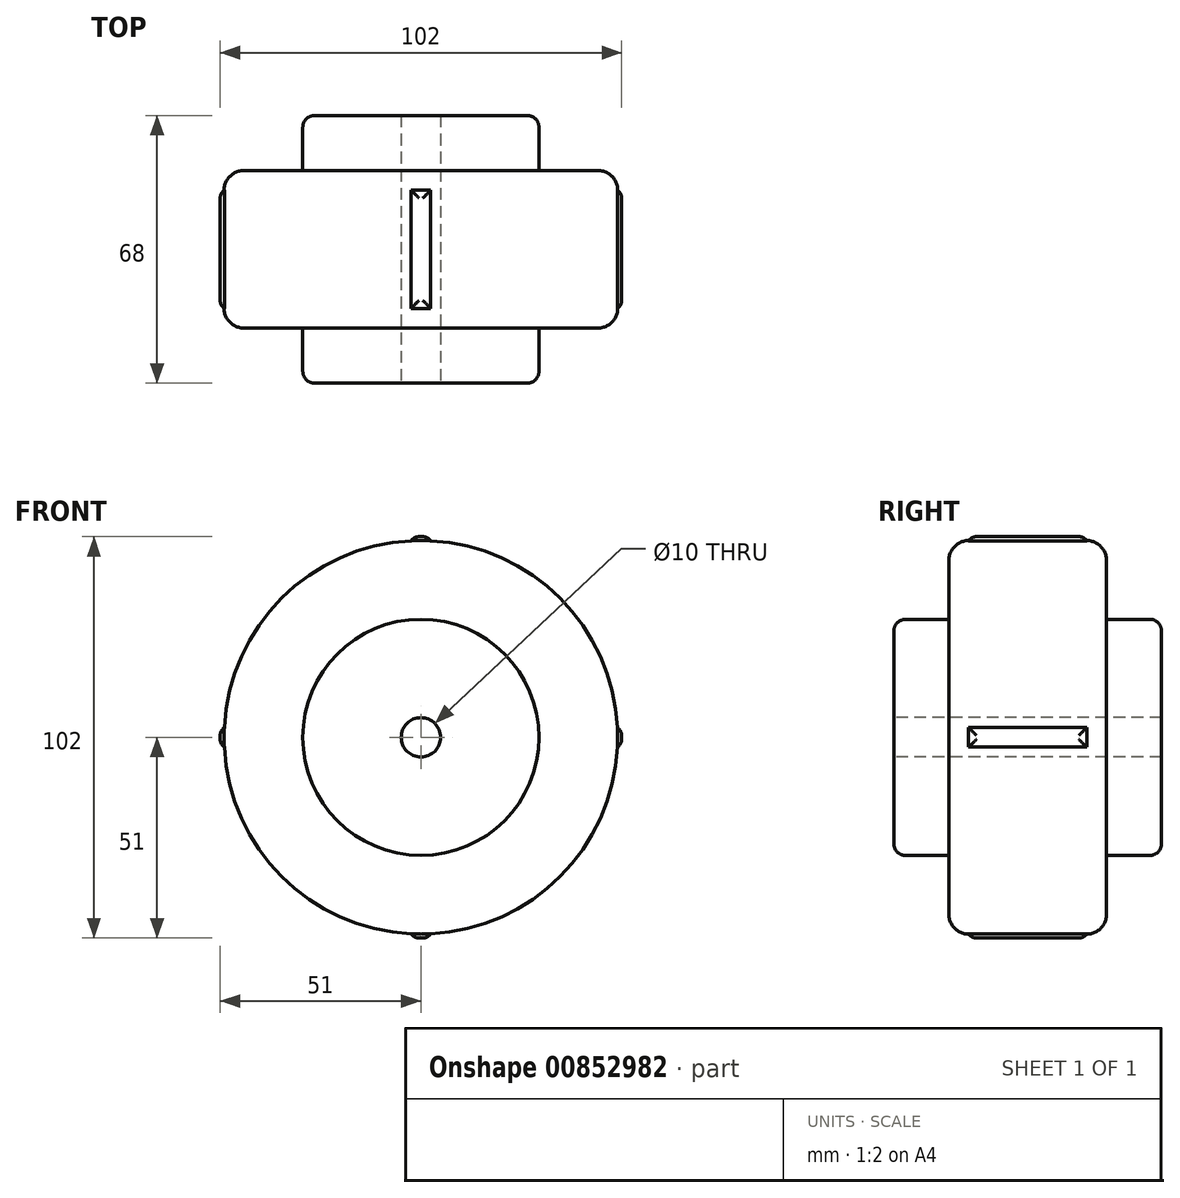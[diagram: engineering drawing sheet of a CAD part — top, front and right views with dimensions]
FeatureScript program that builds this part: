
annotation { "Feature Type Name" : "Feature", "Feature Type Description" : "" }
export const myFeature = defineFeature(function(context is Context, id is Id, definition is map)
    precondition{}
    {
        {
            var Q0;
            Q0=qCreatedBy(makeId("Front.planeOp"),FACE);
            var sketch = newSketch(context, id + "F0", { "sketchPlane" : qUnion([Q0])});
            skPoint(sketch, "E0.third.point", {"position": v(77.43, -43.66) * mm});
            skCircle(sketch, "E1", {"center": v(62.84, 12.63) * mm, "radius": 5 * mm});
            skCircle(sketch, "E2", {"center": v(62.84, 12.63) * mm, "radius": 50 * mm});
            skSolve(sketch);
        }
        {
            var Q0;
            {var subQ0=sQuery(id+"F0.wireOp",EDGE,"eTBRQ0yo-MwLn-4fZX-0Hv7-uYAHV1OEGFlB");Q0=makeQuery(id+"F0.imprint","IMPRINT",FACE,{"disambiguationData":[TD([[makeQuery(id+"F0.imprint","IMPRINT",EDGE,{"derivedFrom":subQ0}),1.0]])]});}
            var Q1;
            Q1=makeQuery(id+"F0.imprint","IMPRINT",FACE,{"disambiguationData":[TD([[makeQuery(id+"F0.imprint","IMPRINT",EDGE,{"derivedFrom":sQuery(id+"F0.wireOp",EDGE,"E1")}),-1.0]])]});
            extrude(context, id + "F1", {"entities" : qUnion([Q0, Q1]), "depth" : 40 * mm, "offsetDistance" : 25 * mm});
        }
        {
            var Q0;
            Q0=makeQuery(id+"F1.opExtrude","CAP_EDGE",EDGE,{"disambiguationData":[OSD([sQuery(id+"F0.wireOp",EDGE,"E2")])],"isStart":true});
            var Q1;
            Q1=makeQuery(id+"F1.opExtrude","CAP_EDGE",EDGE,{"disambiguationData":[OSD([sQuery(id+"F0.wireOp",EDGE,"E2")])],"isStart":false});
            fillet(context, id + "F2", {"entities" : qUnion([Q0, Q1]), "radius" : 5 * mm, "tangentPropagation" : true, "allowEdgeOverflow" : false});
        }
        {
            var Q0;
            Q0=qCreatedBy(makeId("Front.planeOp"),FACE);
            var sketch = newSketch(context, id + "F3", { "sketchPlane" : qUnion([Q0])});
            skArc(sketch, "E3", {"start": v(65.34, 62.57) * mm, "mid": v(62.84, 62.63) * mm, "end": v(60.34, 62.57) * mm});
            skArc(sketch, "E4", {"start": v(65.34, 63.57) * mm, "mid": v(62.84, 63.63) * mm, "end": v(60.34, 63.57) * mm});
            skLineSegment(sketch, "E5.top", {"start": v(62.84, 162.63) * mm, "end": v(60.34, 162.63) * mm});
            skLineSegment(sketch, "E6.top", {"start": v(12.9, 10.13) * mm, "end": v(11.9, 10.13) * mm});
            skLineSegment(sketch, "E7.trimOffspring", {"start": v(112.78, 15.13) * mm, "end": v(113.78, 15.13) * mm});
            skLineSegment(sketch, "E8.trimOffspring", {"start": v(112.78, 10.13) * mm, "end": v(113.78, 10.13) * mm});
            skArc(sketch, "E9.trimOffspring", {"start": v(113.78, 10.13) * mm, "mid": v(113.84, 12.63) * mm, "end": v(113.78, 15.13) * mm});
            skArc(sketch, "E10.trimOffspring", {"start": v(112.78, 10.13) * mm, "mid": v(112.84, 12.63) * mm, "end": v(112.78, 15.13) * mm});
            skLineSegment(sketch, "E11.trimOffspring", {"start": v(60.34, -37.3) * mm, "end": v(60.34, -38.3) * mm});
            skLineSegment(sketch, "E12.trimOffspring", {"start": v(65.34, -37.3) * mm, "end": v(65.34, -38.3) * mm});
            skPoint(sketch, "E13.trimOffspring.end.orphan", {"position": v(62.84, -132.37) * mm});
            skArc(sketch, "E14.trimOffspring", {"start": v(60.34, -38.3) * mm, "mid": v(62.84, -38.37) * mm, "end": v(65.34, -38.3) * mm});
            skArc(sketch, "E15.trimOffspring", {"start": v(60.34, -37.3) * mm, "mid": v(62.84, -37.37) * mm, "end": v(65.34, -37.3) * mm});
            skArc(sketch, "E16.trimOffspring", {"start": v(11.9, 15.13) * mm, "mid": v(11.84, 12.63) * mm, "end": v(11.9, 10.13) * mm});
            skArc(sketch, "E17.trimOffspring", {"start": v(12.9, 15.13) * mm, "mid": v(12.84, 12.63) * mm, "end": v(12.9, 10.13) * mm});
            skLineSegment(sketch, "E18.trimOffspring", {"start": v(12.9, 15.13) * mm, "end": v(11.9, 15.13) * mm});
            skLineSegment(sketch, "E19.trimOffspring", {"start": v(65.34, 62.57) * mm, "end": v(65.34, 63.57) * mm});
            skLineSegment(sketch, "E20.trimOffspring", {"start": v(60.34, 62.57) * mm, "end": v(60.34, 63.57) * mm});
            skSolve(sketch);
        }
        {
            var Q0;
            Q0=makeQuery(id+"F3.imprint","IMPRINT",FACE,{"disambiguationData":[TD([[makeQuery(id+"F3.imprint","IMPRINT",EDGE,{"derivedFrom":sQuery(id+"F3.wireOp",EDGE,"E7.trimOffspring")}),-1.0]])]});
            var Q1;
            Q1=makeQuery(id+"F3.imprint","IMPRINT",FACE,{"disambiguationData":[TD([[makeQuery(id+"F3.imprint","IMPRINT",EDGE,{"derivedFrom":sQuery(id+"F3.wireOp",EDGE,"E11.trimOffspring")}),1.0]])]});
            var Q2;
            Q2=makeQuery(id+"F3.imprint","IMPRINT",FACE,{"disambiguationData":[TD([[makeQuery(id+"F3.imprint","IMPRINT",EDGE,{"derivedFrom":sQuery(id+"F3.wireOp",EDGE,"E6.top")}),-1.0]])]});
            var Q3;
            Q3=makeQuery(id+"F3.imprint","IMPRINT",FACE,{"disambiguationData":[TD([[makeQuery(id+"F3.imprint","IMPRINT",EDGE,{"derivedFrom":sQuery(id+"F3.wireOp",EDGE,"E3")}),-1.0]])]});
            extrude(context, id + "F4", {"entities" : qUnion([Q0, Q1, Q2, Q3]), "operationType" : NewBodyOperationType.ADD, "depth" : 35 * mm, "offsetDistance" : 25 * mm, "hasSecondDirection" : true, "secondDirectionOppositeDirection" : false, "secondDirectionDepth" : 5 * mm});
        }
        {
            var Q0;
            Q0=makeQuery(id+"F4.opExtrude","SWEPT_EDGE",EDGE,{"disambiguationData":[OSD([sQuery(id+"F3.wireOp",EDGE,"E4"),sQuery(id+"F3.wireOp",EDGE,"E19.trimOffspring")])]});
            var Q1;
            Q1=makeQuery(id+"F4.opExtrude","SWEPT_EDGE",EDGE,{"disambiguationData":[OSD([sQuery(id+"F3.wireOp",EDGE,"E4"),sQuery(id+"F3.wireOp",EDGE,"E20.trimOffspring")])]});
            var Q2;
            Q2=makeQuery(id+"F4.opExtrude","SWEPT_EDGE",EDGE,{"disambiguationData":[OSD([sQuery(id+"F3.wireOp",EDGE,"E16.trimOffspring"),sQuery(id+"F3.wireOp",EDGE,"E18.trimOffspring")])]});
            var Q3;
            Q3=makeQuery(id+"F4.opExtrude","SWEPT_EDGE",EDGE,{"disambiguationData":[OSD([sQuery(id+"F3.wireOp",EDGE,"E6.top"),sQuery(id+"F3.wireOp",EDGE,"E16.trimOffspring")])]});
            var Q4;
            Q4=makeQuery(id+"F4.opExtrude","SWEPT_EDGE",EDGE,{"disambiguationData":[OSD([sQuery(id+"F3.wireOp",EDGE,"E11.trimOffspring"),sQuery(id+"F3.wireOp",EDGE,"E14.trimOffspring")])]});
            var Q5;
            Q5=makeQuery(id+"F4.opExtrude","SWEPT_EDGE",EDGE,{"disambiguationData":[OSD([sQuery(id+"F3.wireOp",EDGE,"E12.trimOffspring"),sQuery(id+"F3.wireOp",EDGE,"E14.trimOffspring")])]});
            var Q6;
            Q6=makeQuery(id+"F4.opExtrude","SWEPT_EDGE",EDGE,{"disambiguationData":[OSD([sQuery(id+"F3.wireOp",EDGE,"E8.trimOffspring"),sQuery(id+"F3.wireOp",EDGE,"E9.trimOffspring")])]});
            var Q7;
            Q7=makeQuery(id+"F4.opExtrude","SWEPT_EDGE",EDGE,{"disambiguationData":[OSD([sQuery(id+"F3.wireOp",EDGE,"E7.trimOffspring"),sQuery(id+"F3.wireOp",EDGE,"E9.trimOffspring")])]});
            fillet(context, id + "F5", {"entities" : qUnion([Q0, Q1, Q2, Q3, Q4, Q5, Q6, Q7]), "radius" : 2.5 * mm, "tangentPropagation" : true, "allowEdgeOverflow" : false});
        }
        {
            var Q0;
            Q0=makeQuery(id+"F4.opExtrude","CAP_EDGE",EDGE,{"disambiguationData":[OSD([sQuery(id+"F3.wireOp",EDGE,"E9.trimOffspring")])],"isStart":true});
            var Q1;
            Q1=makeQuery(id+"F4.opExtrude","CAP_EDGE",EDGE,{"disambiguationData":[OSD([sQuery(id+"F3.wireOp",EDGE,"E4")])],"isStart":true});
            var Q2;
            Q2=makeQuery(id+"F4.opExtrude","CAP_EDGE",EDGE,{"disambiguationData":[OSD([sQuery(id+"F3.wireOp",EDGE,"E4")])],"isStart":false});
            var Q3;
            Q3=makeQuery(id+"F4.opExtrude","CAP_EDGE",EDGE,{"disambiguationData":[OSD([sQuery(id+"F3.wireOp",EDGE,"E9.trimOffspring")])],"isStart":false});
            var Q4;
            Q4=makeQuery(id+"F4.opExtrude","CAP_EDGE",EDGE,{"disambiguationData":[OSD([sQuery(id+"F3.wireOp",EDGE,"E14.trimOffspring")])],"isStart":false});
            var Q5;
            Q5=makeQuery(id+"F4.opExtrude","CAP_EDGE",EDGE,{"disambiguationData":[OSD([sQuery(id+"F3.wireOp",EDGE,"E14.trimOffspring")])],"isStart":true});
            var Q6;
            Q6=makeQuery(id+"F4.opExtrude","CAP_EDGE",EDGE,{"disambiguationData":[OSD([sQuery(id+"F3.wireOp",EDGE,"E16.trimOffspring")])],"isStart":false});
            var Q7;
            Q7=makeQuery(id+"F4.opExtrude","CAP_EDGE",EDGE,{"disambiguationData":[OSD([sQuery(id+"F3.wireOp",EDGE,"E16.trimOffspring")])],"isStart":true});
            fillet(context, id + "F6", {"entities" : qUnion([Q0, Q1, Q2, Q3, Q4, Q5, Q6, Q7]), "radius" : 2.5 * mm, "tangentPropagation" : true, "allowEdgeOverflow" : false});
        }
        {
            var Q0;
            Q0=qCreatedBy(makeId("Front.planeOp"),FACE);
            var sketch = newSketch(context, id + "F7", { "sketchPlane" : qUnion([Q0])});
            skCircle(sketch, "E21", {"center": v(62.84, 12.63) * mm, "radius": 30 * mm});
            skSolve(sketch);
        }
        {
            var Q0;
            Q0=makeQuery(id+"F7.imprint","IMPRINT",FACE,{"disambiguationData":[TD([[makeQuery(id+"F7.imprint","IMPRINT",EDGE,{"derivedFrom":sQuery(id+"F7.wireOp",EDGE,"E21")}),1.0]])]});
            extrude(context, id + "F8", {"entities" : qUnion([Q0]), "operationType" : NewBodyOperationType.ADD, "depth" : 54 * mm, "offsetDistance" : 25 * mm, "hasSecondDirection" : true, "secondDirectionOppositeDirection" : true, "secondDirectionDepth" : 14 * mm});
        }
        {
            var Q0;
            Q0=makeQuery(id+"F8.opExtrude","CAP_EDGE",EDGE,{"disambiguationData":[OSD([sQuery(id+"F7.wireOp",EDGE,"E21")])],"isStart":true});
            var Q1;
            Q1=makeQuery(id+"F8.opExtrude","CAP_EDGE",EDGE,{"disambiguationData":[OSD([sQuery(id+"F7.wireOp",EDGE,"E21")])],"isStart":false});
            fillet(context, id + "F9", {"entities" : qUnion([Q0, Q1]), "radius" : 3 * mm, "tangentPropagation" : true, "allowEdgeOverflow" : false});
        }
        {
            var Q0;
            Q0=qCreatedBy(makeId("Front.planeOp"),FACE);
            var sketch = newSketch(context, id + "F10", { "sketchPlane" : qUnion([Q0])});
            skCircle(sketch, "E22", {"center": v(62.84, 12.63) * mm, "radius": 5 * mm});
            skSolve(sketch);
        }
        {
            var Q0;
            Q0=makeQuery(id+"F10.imprint","IMPRINT",FACE,{"disambiguationData":[TD([[makeQuery(id+"F10.imprint","IMPRINT",EDGE,{"derivedFrom":sQuery(id+"F10.wireOp",EDGE,"E22")}),1.0]])]});
            extrude(context, id + "F11", {"entities" : qUnion([Q0]), "operationType" : NewBodyOperationType.REMOVE, "oppositeDirection" : true, "depth" : 37.4 * mm, "offsetDistance" : 25 * mm, "hasSecondDirection" : true, "secondDirectionOppositeDirection" : false, "secondDirectionDepth" : 65.6 * mm});
        }
    });
